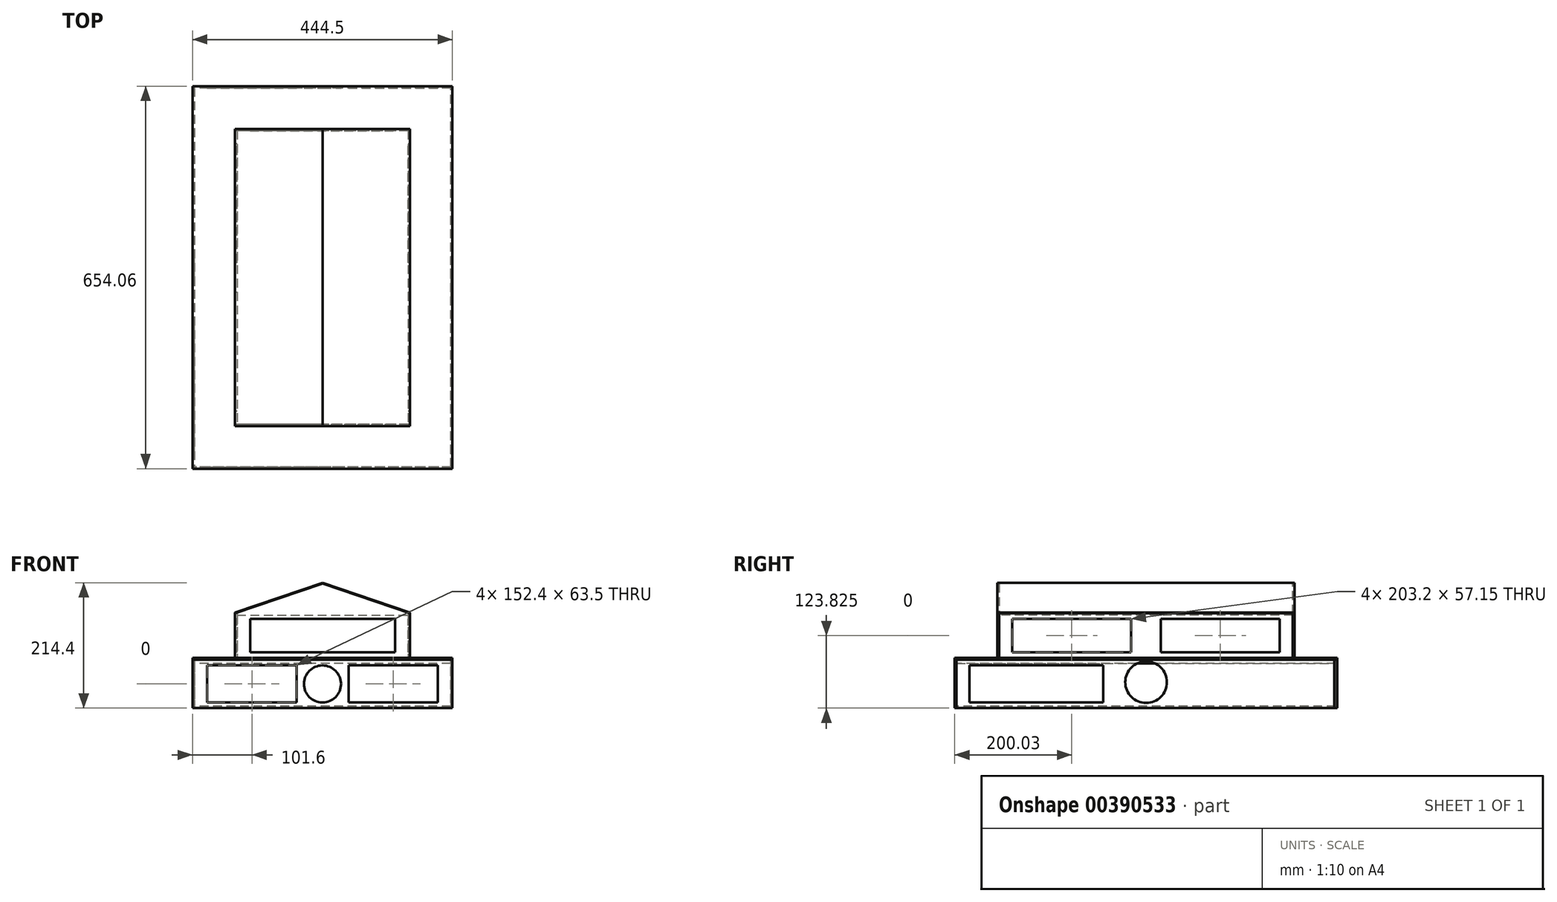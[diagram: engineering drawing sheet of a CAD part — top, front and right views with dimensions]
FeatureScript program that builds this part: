
annotation { "Feature Type Name" : "Feature", "Feature Type Description" : "" }
export const myFeature = defineFeature(function(context is Context, id is Id, definition is map)
    precondition{}
    {
        {
            var Q0;
            Q0=qCreatedBy(makeId("Top.planeOp"),FACE);
            var sketch = newSketch(context, id + "F0", { "sketchPlane" : qUnion([Q0])});
            skLineSegment(sketch, "E0.bottom", {"start": v(219.08, 323.85) * mm, "end": v(-219.07, 323.85) * mm});
            skLineSegment(sketch, "E0.top", {"start": v(219.07, -323.85) * mm, "end": v(-219.08, -323.85) * mm});
            skLineSegment(sketch, "E0.left", {"start": v(219.08, 323.85) * mm, "end": v(219.07, -323.85) * mm});
            skLineSegment(sketch, "E0.right", {"start": v(-219.07, 323.85) * mm, "end": v(-219.08, -323.85) * mm});
            skPoint(sketch, "E0.middle", {"position": v(0, 0) * mm});
            skSolve(sketch);
        }
        {
            var Q0;
            Q0 = qSketchRegion(id + "F0", true);
            extrude(context, id + "F1", {"entities" : qUnion([Q0]), "depth" : 3.17 * mm});
        }
        {
            var Q0;
            Q0=makeQuery(id+"F1.opExtrude","CAP_FACE",FACE,{"disambiguationData":[OSD([sQuery(id+"F0.wireOp",EDGE,"E0.bottom"),sQuery(id+"F0.wireOp",EDGE,"E0.top"),sQuery(id+"F0.wireOp",EDGE,"E0.left"),sQuery(id+"F0.wireOp",EDGE,"E0.right")])],"isStart":true});
            var sketch = newSketch(context, id + "F2", { "sketchPlane" : qUnion([Q0])});
            skLineSegment(sketch, "E1.bottom", {"start": v(222.25, 327.03) * mm, "end": v(-222.25, 327.03) * mm});
            skLineSegment(sketch, "E1.top", {"start": v(222.25, -327.03) * mm, "end": v(-222.25, -327.03) * mm});
            skLineSegment(sketch, "E1.left", {"start": v(222.25, 327.03) * mm, "end": v(222.25, -327.03) * mm});
            skLineSegment(sketch, "E1.right", {"start": v(-222.25, 327.03) * mm, "end": v(-222.25, -327.03) * mm});
            skPoint(sketch, "E1.middle", {"position": v(0, 0) * mm});
            skLineSegment(sketch, "E2.bottom", {"start": v(219.07, 323.85) * mm, "end": v(-219.07, 323.85) * mm});
            skLineSegment(sketch, "E2.top", {"start": v(219.07, -323.85) * mm, "end": v(-219.07, -323.85) * mm});
            skLineSegment(sketch, "E2.left", {"start": v(219.07, 323.85) * mm, "end": v(219.07, -323.85) * mm});
            skLineSegment(sketch, "E2.right", {"start": v(-219.07, 323.85) * mm, "end": v(-219.07, -323.85) * mm});
            skLineSegment(sketch, "E3", {"start": v(219.07, 323.85) * mm, "end": v(222.25, 323.85) * mm});
            skLineSegment(sketch, "E4", {"start": v(-219.07, 323.85) * mm, "end": v(-222.25, 323.85) * mm});
            skLineSegment(sketch, "E5", {"start": v(-219.07, -323.85) * mm, "end": v(-222.25, -323.85) * mm});
            skLineSegment(sketch, "E6", {"start": v(219.07, -323.85) * mm, "end": v(222.25, -321.74) * mm});
            skSolve(sketch);
        }
        {
            var Q0;
            {var subQ1=sQuery(id+"F2.wireOp",EDGE,"E1.bottom");Q0=makeQuery(id+"F2.imprint","IMPRINT",FACE,{"disambiguationData":[TD([[makeQuery(id+"F2.imprint","IMPRINT",EDGE,{"derivedFrom":subQ1}),1.0]])]});}
            var Q1;
            {var subQ1=sQuery(id+"F2.wireOp",EDGE,"E1.top");Q1=makeQuery(id+"F2.imprint","IMPRINT",FACE,{"disambiguationData":[TD([[makeQuery(id+"F2.imprint","IMPRINT",EDGE,{"derivedFrom":subQ1}),-1.0]])]});}
            var Q2;
            Q2=makeQuery(id+"F1.opExtrude","CAP_FACE",FACE,{"disambiguationData":[OSD([sQuery(id+"F0.wireOp",EDGE,"E0.bottom"),sQuery(id+"F0.wireOp",EDGE,"E0.top"),sQuery(id+"F0.wireOp",EDGE,"E0.left"),sQuery(id+"F0.wireOp",EDGE,"E0.right")])],"isStart":false});
            extrude(context, id + "F3", {"entities" : qUnion([Q0, Q1]), "oppositeDirection" : true, "depth" : 82.55 * mm});
        }
        {
            var Q0;
            Q0=makeQuery(id+"F2.imprint","IMPRINT",FACE,{"disambiguationData":[TD([[makeQuery(id+"F2.imprint","IMPRINT",EDGE,{"derivedFrom":sQuery(id+"F2.wireOp",EDGE,"E2.left")}),-1.0]])]});
            var Q1;
            Q1=makeQuery(id+"F2.imprint","IMPRINT",FACE,{"disambiguationData":[TD([[makeQuery(id+"F2.imprint","IMPRINT",EDGE,{"derivedFrom":sQuery(id+"F2.wireOp",EDGE,"E2.right")}),1.0]])]});
            var Q2;
            Q2=makeQuery(id+"F3.opExtrude","CAP_FACE",FACE,{"disambiguationData":[OSD([sQuery(id+"F2.wireOp",EDGE,"E1.top"),sQuery(id+"F2.wireOp",EDGE,"E1.left"),sQuery(id+"F2.wireOp",EDGE,"E1.right"),sQuery(id+"F2.wireOp",EDGE,"E2.top"),sQuery(id+"F2.wireOp",EDGE,"E5"),sQuery(id+"F2.wireOp",EDGE,"E6")])],"isStart":false});
            extrude(context, id + "F4", {"entities" : qUnion([Q0, Q1]), "endBound" : BoundingType.UP_TO_SURFACE, "oppositeDirection" : true, "endBoundEntityFace" : qUnion([Q2]), "depth" : 25.4 * mm});
        }
        {
            var Q0;
            Q0=makeQuery(id+"F4.opExtrude","SWEPT_FACE",FACE,{"disambiguationData":[OSD([sQuery(id+"F2.wireOp",EDGE,"E1.right")])]});
            var sketch = newSketch(context, id + "F5", { "sketchPlane" : qUnion([Q0])});
            skCircle(sketch, "E7", {"center": v(0, 44.45) * mm, "radius": 35.56 * mm});
            skSolve(sketch);
        }
        {
            var Q0;
            Q0=makeQuery(id+"F5.imprint","IMPRINT",FACE,{"disambiguationData":[TD([[makeQuery(id+"F5.imprint","IMPRINT",EDGE,{"derivedFrom":sQuery(id+"F5.wireOp",EDGE,"E7")}),1.0]])]});
            extrude(context, id + "F6", {"entities" : qUnion([Q0]), "operationType" : NewBodyOperationType.REMOVE, "endBound" : BoundingType.THROUGH_ALL, "oppositeDirection" : true, "depth" : 25.4 * mm});
        }
        {
            var Q0;
            Q0=makeQuery(id+"F4.opExtrude","SWEPT_FACE",FACE,{"disambiguationData":[OSD([sQuery(id+"F2.wireOp",EDGE,"E1.right")])]});
            var sketch = newSketch(context, id + "F7", { "sketchPlane" : qUnion([Q0])});
            skLineSegment(sketch, "E8.bottom", {"start": v(200.03, 73.03) * mm, "end": v(301.63, 73.03) * mm});
            skLineSegment(sketch, "E8.top", {"start": v(200.03, 47.63) * mm, "end": v(301.63, 47.63) * mm});
            skLineSegment(sketch, "E8.left", {"start": v(200.03, 73.03) * mm, "end": v(200.03, 47.63) * mm});
            skLineSegment(sketch, "E8.right", {"start": v(301.63, 73.03) * mm, "end": v(301.63, 47.63) * mm});
            skLineSegment(sketch, "E9.bottom", {"start": v(263.53, 34.92) * mm, "end": v(301.63, 34.92) * mm});
            skLineSegment(sketch, "E9.top", {"start": v(263.53, 9.53) * mm, "end": v(301.63, 9.53) * mm});
            skLineSegment(sketch, "E9.left", {"start": v(263.53, 34.92) * mm, "end": v(263.53, 9.52) * mm});
            skLineSegment(sketch, "E9.right", {"start": v(301.63, 34.92) * mm, "end": v(301.63, 9.52) * mm});
            skLineSegment(sketch, "E10", {"start": v(250.83, 47.63) * mm, "end": v(250.83, 34.92) * mm, "construction": true});
            skLineSegment(sketch, "E11", {"start": v(250.83, 34.92) * mm, "end": v(263.53, 34.92) * mm, "construction": true});
            skLineSegment(sketch, "E12.bottom", {"start": v(238.13, 34.92) * mm, "end": v(136.53, 34.92) * mm});
            skLineSegment(sketch, "E12.top", {"start": v(238.13, 9.53) * mm, "end": v(136.53, 9.52) * mm});
            skLineSegment(sketch, "E12.left", {"start": v(238.13, 34.92) * mm, "end": v(238.13, 9.53) * mm});
            skLineSegment(sketch, "E12.right", {"start": v(136.53, 34.92) * mm, "end": v(136.53, 9.52) * mm});
            skLineSegment(sketch, "E13", {"start": v(238.13, 34.92) * mm, "end": v(250.83, 34.92) * mm, "construction": true});
            skLineSegment(sketch, "E14", {"start": v(263.53, 9.53) * mm, "end": v(263.53, 0) * mm, "construction": true});
            skLineSegment(sketch, "E15", {"start": v(250.83, 73.03) * mm, "end": v(250.83, 82.55) * mm, "construction": true});
            skLineSegment(sketch, "E16.bottom", {"start": v(174.63, 73.03) * mm, "end": v(73.03, 73.03) * mm});
            skLineSegment(sketch, "E16.top", {"start": v(174.63, 47.63) * mm, "end": v(73.03, 47.63) * mm});
            skLineSegment(sketch, "E16.left", {"start": v(174.63, 73.03) * mm, "end": v(174.63, 47.63) * mm});
            skLineSegment(sketch, "E16.right", {"start": v(73.03, 73.03) * mm, "end": v(73.03, 47.63) * mm});
            skLineSegment(sketch, "E17", {"start": v(174.63, 60.33) * mm, "end": v(187.33, 60.33) * mm, "construction": true});
            skLineSegment(sketch, "E18", {"start": v(187.33, 60.33) * mm, "end": v(200.03, 60.33) * mm, "construction": true});
            skLineSegment(sketch, "E19.bottom", {"start": v(73.03, 34.92) * mm, "end": v(111.13, 34.92) * mm});
            skLineSegment(sketch, "E19.top", {"start": v(73.03, 9.52) * mm, "end": v(111.13, 9.52) * mm});
            skLineSegment(sketch, "E19.left", {"start": v(73.03, 34.92) * mm, "end": v(73.03, 9.52) * mm});
            skLineSegment(sketch, "E19.right", {"start": v(111.13, 34.92) * mm, "end": v(111.13, 9.52) * mm});
            skLineSegment(sketch, "E20", {"start": v(174.63, 73.03) * mm, "end": v(200.03, 73.03) * mm});
            skLineSegment(sketch, "E21", {"start": v(111.13, 9.52) * mm, "end": v(136.53, 9.52) * mm});
            skLineSegment(sketch, "E22", {"start": v(73.03, 34.92) * mm, "end": v(73.03, 47.63) * mm});
            skLineSegment(sketch, "E23", {"start": v(301.63, 47.63) * mm, "end": v(301.63, 34.92) * mm});
            skLineSegment(sketch, "E24", {"start": v(238.13, 9.53) * mm, "end": v(263.53, 9.53) * mm});
            skSolve(sketch);
        }
        {
            var Q0;
            Q0 = qSketchRegion(id + "F7", true);
            extrude(context, id + "F8", {"entities" : qUnion([Q0]), "operationType" : NewBodyOperationType.REMOVE, "endBound" : BoundingType.THROUGH_ALL, "oppositeDirection" : true, "depth" : 25.4 * mm});
        }
        {
            var Q0;
            Q0=makeQuery(id+"F3.opExtrude","SWEPT_FACE",FACE,{"disambiguationData":[OSD([sQuery(id+"F2.wireOp",EDGE,"E1.bottom")])]});
            var sketch = newSketch(context, id + "F9", { "sketchPlane" : qUnion([Q0])});
            skLineSegment(sketch, "E25.bottom", {"start": v(-196.85, 73.03) * mm, "end": v(196.85, 73.03) * mm});
            skLineSegment(sketch, "E25.top", {"start": v(-196.85, 9.52) * mm, "end": v(196.85, 9.52) * mm});
            skLineSegment(sketch, "E25.left", {"start": v(-196.85, 73.03) * mm, "end": v(-196.85, 9.52) * mm});
            skLineSegment(sketch, "E25.right", {"start": v(196.85, 73.03) * mm, "end": v(196.85, 9.52) * mm});
            skPoint(sketch, "E25.middle", {"position": v(0, 41.28) * mm});
            skLineSegment(sketch, "E26.bottom", {"start": v(6.35, 73.03) * mm, "end": v(-6.35, 73.03) * mm});
            skLineSegment(sketch, "E26.top", {"start": v(6.35, 9.52) * mm, "end": v(-6.35, 9.52) * mm});
            skLineSegment(sketch, "E26.left", {"start": v(6.35, 73.03) * mm, "end": v(6.35, 9.52) * mm});
            skLineSegment(sketch, "E26.right", {"start": v(-6.35, 73.03) * mm, "end": v(-6.35, 9.52) * mm});
            skCircle(sketch, "E27", {"center": v(0, 41.28) * mm, "radius": 31.75 * mm});
            skLineSegment(sketch, "E28.bottom", {"start": v(44.45, 73.03) * mm, "end": v(-44.45, 73.03) * mm});
            skLineSegment(sketch, "E28.top", {"start": v(44.45, 9.52) * mm, "end": v(-44.45, 9.52) * mm});
            skLineSegment(sketch, "E28.left", {"start": v(44.45, 73.03) * mm, "end": v(44.45, 9.52) * mm});
            skLineSegment(sketch, "E28.right", {"start": v(-44.45, 73.03) * mm, "end": v(-44.45, 9.52) * mm});
            skSolve(sketch);
        }
        {
            var Q0;
            {var subQ0=sQuery(id+"F9.wireOp",EDGE,"E25.left");Q0=makeQuery(id+"F9.imprint","IMPRINT",FACE,{"disambiguationData":[TD([[makeQuery(id+"F9.imprint","IMPRINT",EDGE,{"derivedFrom":subQ0}),1.0]])]});}
            var Q1;
            {var subQ0=sQuery(id+"F9.wireOp",EDGE,"E25.right");Q1=makeQuery(id+"F9.imprint","IMPRINT",FACE,{"disambiguationData":[TD([[makeQuery(id+"F9.imprint","IMPRINT",EDGE,{"derivedFrom":subQ0}),-1.0]])]});}
            var Q2;
            {var subQ0=sQuery(id+"F9.wireOp",EDGE,"E27");var subQ1=sQuery(id+"F9.wireOp",EDGE,"E26.right");var subQ2=makeQuery(id+"F9.imprint","INTERSECT",VERTEX,{"disambiguationData":[OD(0.0)],"derivedFrom":[subQ1,subQ0]});Q2=makeQuery(id+"F9.imprint","IMPRINT",FACE,{"disambiguationData":[TD([[makeQuery(id+"F9.imprint","IMPRINT",EDGE,{"disambiguationData":[TD([[subQ2,-1.0]])],"derivedFrom":subQ1}),-1.0]])]});}
            var Q3;
            {var subQ0=sQuery(id+"F9.wireOp",EDGE,"E27");var subQ5=sQuery(id+"F9.wireOp",EDGE,"E26.left");var subQ6=makeQuery(id+"F9.imprint","INTERSECT",VERTEX,{"disambiguationData":[OD(0.0)],"derivedFrom":[subQ5,subQ0]});Q3=makeQuery(id+"F9.imprint","IMPRINT",FACE,{"disambiguationData":[TD([[makeQuery(id+"F9.imprint","IMPRINT",EDGE,{"disambiguationData":[TD([[subQ6,-1.0]])],"derivedFrom":subQ5}),-1.0]])]});}
            var Q4;
            {var subQ0=sQuery(id+"F9.wireOp",EDGE,"E27");var subQ1=sQuery(id+"F9.wireOp",EDGE,"E26.left");var subQ2=makeQuery(id+"F9.imprint","INTERSECT",VERTEX,{"disambiguationData":[OD(0.0)],"derivedFrom":[subQ1,subQ0]});Q4=makeQuery(id+"F9.imprint","IMPRINT",FACE,{"disambiguationData":[TD([[makeQuery(id+"F9.imprint","IMPRINT",EDGE,{"disambiguationData":[TD([[subQ2,-1.0]])],"derivedFrom":subQ1}),1.0]])]});}
            extrude(context, id + "F10", {"entities" : qUnion([Q0, Q1, Q2, Q3, Q4]), "operationType" : NewBodyOperationType.REMOVE, "endBound" : BoundingType.THROUGH_ALL, "oppositeDirection" : true, "depth" : 25.4 * mm});
        }
        {
            var Q0;
            Q0=makeQuery(id+"F3.opExtrude","CAP_FACE",FACE,{"disambiguationData":[OSD([sQuery(id+"F2.wireOp",EDGE,"E1.bottom"),sQuery(id+"F2.wireOp",EDGE,"E1.left"),sQuery(id+"F2.wireOp",EDGE,"E1.right"),sQuery(id+"F2.wireOp",EDGE,"E2.bottom"),sQuery(id+"F2.wireOp",EDGE,"E3"),sQuery(id+"F2.wireOp",EDGE,"E4")])],"isStart":false});
            var sketch = newSketch(context, id + "F11", { "sketchPlane" : qUnion([Q0])});
            skLineSegment(sketch, "E29.bottom", {"start": v(-222.25, -327.03) * mm, "end": v(222.25, -327.03) * mm});
            skLineSegment(sketch, "E29.top", {"start": v(-222.25, 327.03) * mm, "end": v(222.25, 327.03) * mm});
            skLineSegment(sketch, "E29.left", {"start": v(-222.25, -327.03) * mm, "end": v(-222.25, 327.03) * mm});
            skLineSegment(sketch, "E29.right", {"start": v(222.25, -327.03) * mm, "end": v(222.25, 327.03) * mm});
            skSolve(sketch);
        }
        {
            var Q0;
            Q0 = qSketchRegion(id + "F11", true);
            extrude(context, id + "F12", {"entities" : qUnion([Q0]), "depth" : 3.17 * mm});
        }
        {
            var Q0;
            Q0=makeQuery(id+"F12.opExtrude","CAP_FACE",FACE,{"disambiguationData":[OSD([sQuery(id+"F11.wireOp",EDGE,"E29.bottom"),sQuery(id+"F11.wireOp",EDGE,"E29.top"),sQuery(id+"F11.wireOp",EDGE,"E29.left"),sQuery(id+"F11.wireOp",EDGE,"E29.right")])],"isStart":false});
            var sketch = newSketch(context, id + "F13", { "sketchPlane" : qUnion([Q0])});
            skLineSegment(sketch, "E30.bottom", {"start": v(-146.05, 250.83) * mm, "end": v(146.05, 250.83) * mm});
            skLineSegment(sketch, "E30.top", {"start": v(-146.05, -250.83) * mm, "end": v(146.05, -250.83) * mm});
            skLineSegment(sketch, "E30.left", {"start": v(-146.05, 250.83) * mm, "end": v(-146.05, -250.83) * mm});
            skLineSegment(sketch, "E30.right", {"start": v(146.05, 250.83) * mm, "end": v(146.05, -250.83) * mm});
            skPoint(sketch, "E30.middle", {"position": v(0, 0) * mm});
            skSolve(sketch);
        }
        {
            var Q0;
            Q0=makeQuery(id+"F13.imprint","IMPRINT",FACE,{"disambiguationData":[TD([[makeQuery(id+"F13.imprint","IMPRINT",EDGE,{"derivedFrom":sQuery(id+"F13.wireOp",EDGE,"E30.bottom")}),-1.0]])]});
            extrude(context, id + "F14", {"entities" : qUnion([Q0]), "operationType" : NewBodyOperationType.REMOVE, "oppositeDirection" : true, "depth" : 25.4 * mm});
        }
        {
            var Q0;
            Q0=makeQuery(id+"F12.opExtrude","CAP_FACE",FACE,{"disambiguationData":[OSD([sQuery(id+"F11.wireOp",EDGE,"E29.bottom"),sQuery(id+"F11.wireOp",EDGE,"E29.top"),sQuery(id+"F11.wireOp",EDGE,"E29.left"),sQuery(id+"F11.wireOp",EDGE,"E29.right")])],"isStart":false});
            var sketch = newSketch(context, id + "F15", { "sketchPlane" : qUnion([Q0])});
            skLineSegment(sketch, "E31.bottom", {"start": v(-146.05, 250.83) * mm, "end": v(146.05, 250.83) * mm});
            skLineSegment(sketch, "E31.top", {"start": v(-146.05, -250.83) * mm, "end": v(146.05, -250.83) * mm});
            skLineSegment(sketch, "E31.left", {"start": v(-146.05, 250.83) * mm, "end": v(-146.05, -250.83) * mm});
            skLineSegment(sketch, "E31.right", {"start": v(146.05, 250.83) * mm, "end": v(146.05, -250.83) * mm});
            skPoint(sketch, "E31.middle", {"position": v(0, 0) * mm});
            skLineSegment(sketch, "E32.bottom", {"start": v(-149.22, 254) * mm, "end": v(149.22, 254) * mm});
            skLineSegment(sketch, "E32.top", {"start": v(-149.22, -254) * mm, "end": v(149.22, -254) * mm});
            skLineSegment(sketch, "E32.left", {"start": v(-149.22, 254) * mm, "end": v(-149.22, -254) * mm});
            skLineSegment(sketch, "E32.right", {"start": v(149.22, 254) * mm, "end": v(149.22, -254) * mm});
            skLineSegment(sketch, "E33", {"start": v(-146.05, 250.83) * mm, "end": v(-149.22, 250.83) * mm});
            skLineSegment(sketch, "E34", {"start": v(146.05, 250.83) * mm, "end": v(149.22, 250.83) * mm});
            skLineSegment(sketch, "E35", {"start": v(-146.05, -250.83) * mm, "end": v(-149.22, -250.83) * mm});
            skLineSegment(sketch, "E36", {"start": v(-149.22, -250.83) * mm, "end": v(146.05, -250.83) * mm});
            skLineSegment(sketch, "E37", {"start": v(146.05, -250.83) * mm, "end": v(149.22, -250.83) * mm});
            skSolve(sketch);
        }
        {
            var Q0;
            {var subQ5=sQuery(id+"F15.wireOp",EDGE,"E32.top");Q0=makeQuery(id+"F15.imprint","IMPRINT",FACE,{"disambiguationData":[TD([[makeQuery(id+"F15.imprint","IMPRINT",EDGE,{"derivedFrom":subQ5}),1.0]])]});}
            extrude(context, id + "F16", {"entities" : qUnion([Q0]), "depth" : 76.2 * mm});
        }
        {
            var Q0;
            {var subQ0=sQuery(id+"F15.wireOp",EDGE,"E31.left");Q0=makeQuery(id+"F15.imprint","IMPRINT",FACE,{"disambiguationData":[TD([[makeQuery(id+"F15.imprint","IMPRINT",EDGE,{"derivedFrom":subQ0}),-1.0]])]});}
            var Q1;
            Q1=makeQuery(id+"F15.imprint","IMPRINT",FACE,{"disambiguationData":[TD([[makeQuery(id+"F15.imprint","IMPRINT",EDGE,{"derivedFrom":sQuery(id+"F15.wireOp",EDGE,"E31.right")}),1.0]])]});
            var Q2;
            Q2=makeQuery(id+"F16.opExtrude","CAP_FACE",FACE,{"disambiguationData":[OSD([sQuery(id+"F15.wireOp",EDGE,"E32.top"),sQuery(id+"F15.wireOp",EDGE,"E32.left"),sQuery(id+"F15.wireOp",EDGE,"E32.right"),sQuery(id+"F15.wireOp",EDGE,"E36"),sQuery(id+"F15.wireOp",EDGE,"E37")])],"isStart":false});
            extrude(context, id + "F17", {"entities" : qUnion([Q0, Q1]), "endBound" : BoundingType.UP_TO_SURFACE, "endBoundEntityFace" : qUnion([Q2]), "depth" : 25.4 * mm});
        }
        {
            var Q0;
            Q0=makeQuery(id+"F16.opExtrude","SWEPT_FACE",FACE,{"disambiguationData":[OSD([sQuery(id+"F15.wireOp",EDGE,"E32.top")])]});
            var sketch = newSketch(context, id + "F18", { "sketchPlane" : qUnion([Q0])});
            skLineSegment(sketch, "E38", {"start": v(-149.22, 161.93) * mm, "end": v(149.22, 85.72) * mm});
            skLineSegment(sketch, "E39.bottom", {"start": v(-123.82, 95.25) * mm, "end": v(123.82, 95.25) * mm});
            skLineSegment(sketch, "E39.top", {"start": v(-123.82, 152.4) * mm, "end": v(123.82, 152.4) * mm});
            skLineSegment(sketch, "E39.left", {"start": v(-123.82, 95.25) * mm, "end": v(-123.82, 152.4) * mm});
            skLineSegment(sketch, "E39.right", {"start": v(123.82, 95.25) * mm, "end": v(123.82, 152.4) * mm});
            skPoint(sketch, "E39.middle", {"position": v(0, 123.83) * mm});
            skSolve(sketch);
        }
        {
            var Q0;
            {var subQ5=sQuery(id+"F18.wireOp",EDGE,"E39.left");Q0=makeQuery(id+"F18.imprint","IMPRINT",FACE,{"disambiguationData":[TD([[makeQuery(id+"F18.imprint","IMPRINT",EDGE,{"derivedFrom":subQ5}),-1.0]])]});}
            var Q1;
            {var subQ5=sQuery(id+"F18.wireOp",EDGE,"E39.right");Q1=makeQuery(id+"F18.imprint","IMPRINT",FACE,{"disambiguationData":[TD([[makeQuery(id+"F18.imprint","IMPRINT",EDGE,{"derivedFrom":subQ5}),1.0]])]});}
            extrude(context, id + "F19", {"entities" : qUnion([Q0, Q1]), "operationType" : NewBodyOperationType.REMOVE, "endBound" : BoundingType.THROUGH_ALL, "oppositeDirection" : true, "depth" : 25.4 * mm});
        }
        {
            var Q0;
            Q0=makeQuery(id+"F17.opExtrude","SWEPT_FACE",FACE,{"disambiguationData":[OSD([sQuery(id+"F15.wireOp",EDGE,"E32.left")])]});
            var sketch = newSketch(context, id + "F20", { "sketchPlane" : qUnion([Q0])});
            skLineSegment(sketch, "E40.bottom", {"start": v(228.6, 152.4) * mm, "end": v(25.4, 152.4) * mm});
            skLineSegment(sketch, "E40.top", {"start": v(228.6, 95.25) * mm, "end": v(25.4, 95.25) * mm});
            skLineSegment(sketch, "E40.left", {"start": v(228.6, 152.4) * mm, "end": v(228.6, 95.25) * mm});
            skLineSegment(sketch, "E40.right", {"start": v(25.4, 152.4) * mm, "end": v(25.4, 95.25) * mm});
            skPoint(sketch, "E40.middle", {"position": v(127, 123.83) * mm});
            skLineSegment(sketch, "E41", {"start": v(0, 161.92) * mm, "end": v(0, 85.73) * mm});
            skSolve(sketch);
        }
        {
            var Q0;
            Q0=makeQuery(id+"F20.imprint","IMPRINT",FACE,{"disambiguationData":[TD([[makeQuery(id+"F20.imprint","IMPRINT",EDGE,{"derivedFrom":sQuery(id+"F20.wireOp",EDGE,"E40.bottom")}),1.0]])]});
            extrude(context, id + "F21", {"entities" : qUnion([Q0]), "operationType" : NewBodyOperationType.REMOVE, "endBound" : BoundingType.THROUGH_ALL, "oppositeDirection" : true, "depth" : 25.4 * mm});
        }
        {
            var Q0;
            Q0=makeQuery(id+"F16.opExtrude","SWEPT_FACE",FACE,{"disambiguationData":[OSD([sQuery(id+"F15.wireOp",EDGE,"E32.top")])]});
            var sketch = newSketch(context, id + "F22", { "sketchPlane" : qUnion([Q0])});
            skLineSegment(sketch, "E42", {"start": v(-149.22, 161.92) * mm, "end": v(0, 212.73) * mm});
            skLineSegment(sketch, "E43", {"start": v(0, 212.73) * mm, "end": v(149.22, 161.93) * mm});
            skLineSegment(sketch, "E44", {"start": v(149.22, 161.93) * mm, "end": v(-149.22, 161.93) * mm});
            skLineSegment(sketch, "E45", {"start": v(0, 212.73) * mm, "end": v(0, 161.92) * mm});
            skSolve(sketch);
        }
        {
            var Q0;
            {var subQ0=sQuery(id+"F22.wireOp",EDGE,"E42");Q0=makeQuery(id+"F22.imprint","IMPRINT",FACE,{"disambiguationData":[TD([[makeQuery(id+"F22.imprint","IMPRINT",EDGE,{"derivedFrom":subQ0}),-1.0]])]});}
            var Q1;
            {var subQ0=sQuery(id+"F22.wireOp",EDGE,"E43");Q1=makeQuery(id+"F22.imprint","IMPRINT",FACE,{"disambiguationData":[TD([[makeQuery(id+"F22.imprint","IMPRINT",EDGE,{"derivedFrom":subQ0}),-1.0]])]});}
            var Q2;
            Q2=makeQuery(id+"F16.opExtrude","SWEPT_FACE",FACE,{"disambiguationData":[OSD([sQuery(id+"F15.wireOp",EDGE,"E36"),sQuery(id+"F15.wireOp",EDGE,"E37")])]});
            extrude(context, id + "F23", {"entities" : qUnion([Q0, Q1]), "operationType" : NewBodyOperationType.ADD, "endBound" : BoundingType.UP_TO_SURFACE, "oppositeDirection" : true, "endBoundEntityFace" : qUnion([Q2]), "depth" : 25.4 * mm});
        }
        {
            var Q0;
            Q0=makeQuery(id+"F23.boolean.opBoolean","MERGE",FACE,{"derivedFrom":[makeQuery(id+"F16.opExtrude","SWEPT_FACE",FACE,{"disambiguationData":[OSD([sQuery(id+"F15.wireOp",EDGE,"E32.top")])]}),makeQuery(id+"F23.opExtrude","CAP_FACE",FACE,{"disambiguationData":[OSD([sQuery(id+"F22.wireOp",EDGE,"E42"),sQuery(id+"F22.wireOp",EDGE,"E43"),sQuery(id+"F22.wireOp",EDGE,"E44")])],"isStart":true})]});
            var sketch = newSketch(context, id + "F24", { "sketchPlane" : qUnion([Q0])});
            skLineSegment(sketch, "E46", {"start": v(-149.22, 161.93) * mm, "end": v(0, 212.73) * mm});
            skLineSegment(sketch, "E47", {"start": v(0, 212.73) * mm, "end": v(149.22, 161.93) * mm});
            skLineSegment(sketch, "E48", {"start": v(149.22, 161.93) * mm, "end": v(149.74, 163.43) * mm});
            skLineSegment(sketch, "E49", {"start": v(149.74, 163.43) * mm, "end": v(0, 214.4) * mm});
            skLineSegment(sketch, "E50", {"start": v(0, 214.4) * mm, "end": v(-149.74, 163.43) * mm});
            skLineSegment(sketch, "E51", {"start": v(-149.74, 163.43) * mm, "end": v(-149.22, 161.93) * mm});
            skSolve(sketch);
        }
        {
            var Q0;
            Q0=makeQuery(id+"F16.opExtrude","SWEPT_BODY",BODY,{"disambiguationData":[OSD([sQuery(id+"F15.wireOp",EDGE,"E32.top"),sQuery(id+"F15.wireOp",EDGE,"E32.left"),sQuery(id+"F15.wireOp",EDGE,"E32.right"),sQuery(id+"F15.wireOp",EDGE,"E36"),sQuery(id+"F15.wireOp",EDGE,"E37")])]});
            var Q1;
            Q1=qCreatedBy(makeId("Front.planeOp"),FACE);
            mirror(context, id + "F25", {"entities" : qUnion([Q0]), "mirrorPlane" : qUnion([Q1])});
        }
        {
            var Q0;
            Q0=makeQuery(id+"F24.imprint","IMPRINT",FACE,{"disambiguationData":[TD([[makeQuery(id+"F24.imprint","IMPRINT",EDGE,{"derivedFrom":sQuery(id+"F24.wireOp",EDGE,"E46")}),1.0]])]});
            var Q1;
            Q1=makeQuery(id+"F25.opPattern","COPY",FACE,{"derivedFrom":makeQuery(id+"F23.boolean.opBoolean","MERGE",FACE,{"derivedFrom":[makeQuery(id+"F16.opExtrude","SWEPT_FACE",FACE,{"disambiguationData":[OSD([sQuery(id+"F15.wireOp",EDGE,"E32.top")])]}),makeQuery(id+"F23.opExtrude","CAP_FACE",FACE,{"disambiguationData":[OSD([sQuery(id+"F22.wireOp",EDGE,"E42"),sQuery(id+"F22.wireOp",EDGE,"E43"),sQuery(id+"F22.wireOp",EDGE,"E44")])],"isStart":true})]}),"instanceName":"1"});
            extrude(context, id + "F26", {"entities" : qUnion([Q0]), "endBound" : BoundingType.UP_TO_SURFACE, "oppositeDirection" : true, "endBoundEntityFace" : qUnion([Q1]), "depth" : 25.4 * mm});
        }
        {
            var Q0;
            Q0=makeQuery(id+"F12.opExtrude","CAP_FACE",FACE,{"disambiguationData":[OSD([sQuery(id+"F11.wireOp",EDGE,"E29.bottom"),sQuery(id+"F11.wireOp",EDGE,"E29.top"),sQuery(id+"F11.wireOp",EDGE,"E29.left"),sQuery(id+"F11.wireOp",EDGE,"E29.right")])],"isStart":true});
            var sketch = newSketch(context, id + "F27", { "sketchPlane" : qUnion([Q0])});
            skLineSegment(sketch, "E52.bottom", {"start": v(146.05, -250.83) * mm, "end": v(-146.05, -250.83) * mm});
            skLineSegment(sketch, "E52.top", {"start": v(146.05, 250.83) * mm, "end": v(-146.05, 250.82) * mm});
            skLineSegment(sketch, "E52.left", {"start": v(146.05, -250.83) * mm, "end": v(146.05, 250.83) * mm});
            skLineSegment(sketch, "E52.right", {"start": v(-146.05, -250.83) * mm, "end": v(-146.05, 250.83) * mm});
            skSolve(sketch);
        }
        {
            var Q0;
            Q0 = qSketchRegion(id + "F27", true);
            extrude(context, id + "F28", {"entities" : qUnion([Q0]), "oppositeDirection" : true, "depth" : 76.2 * mm});
        }
        {
            var Q0;
            Q0=makeQuery(id+"F4.opExtrude","CAP_FACE",FACE,{"disambiguationData":[OSD([sQuery(id+"F2.wireOp",EDGE,"E1.left"),sQuery(id+"F2.wireOp",EDGE,"E2.left"),sQuery(id+"F2.wireOp",EDGE,"E3"),sQuery(id+"F2.wireOp",EDGE,"E6")])],"isStart":true});
            var sketch = newSketch(context, id + "F29", { "sketchPlane" : qUnion([Q0])});
            skLineSegment(sketch, "E53.bottom", {"start": v(219.07, 323.85) * mm, "end": v(-219.08, 323.85) * mm});
            skLineSegment(sketch, "E53.top", {"start": v(219.08, -323.85) * mm, "end": v(-219.07, -323.85) * mm});
            skLineSegment(sketch, "E53.left", {"start": v(219.07, 323.85) * mm, "end": v(219.08, -323.85) * mm});
            skLineSegment(sketch, "E53.right", {"start": v(-219.08, 323.85) * mm, "end": v(-219.07, -323.85) * mm});
            skSolve(sketch);
        }
        {
            var Q0;
            Q0 = qSketchRegion(id + "F29", true);
            extrude(context, id + "F30", {"entities" : qUnion([Q0]), "oppositeDirection" : true, "depth" : 76.2 * mm});
        }
    });
